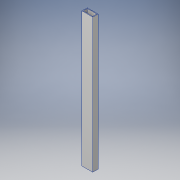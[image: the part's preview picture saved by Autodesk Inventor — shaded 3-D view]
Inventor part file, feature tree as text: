
AUTODESK INVENTOR PART (.ipt)
format: ipt  version: 2018 (Build 220112000, 112)  size: 110,080 bytes
history: native  units: in
note: dims shown in document units (in); Inventor stores cm internally (conversion verified against a paired STEP export)
features: extrude x2, sketch x2
ambient origin geometry x8: Origin, YZ Plane, XZ Plane, XY Plane, X Axis, Y Axis, Z Axis, Center Point
bodies: Solid1 (feature_tree)
feature tree (4):
  extrude  "Extrusion1"  Depth=2.0in
  extrude  "Extrusion2"  Depth=0.125in
  sketch  "Sketch1"  dims[d0=1.0in d1=2.0in]
  sketch  "Sketch2"  dims[d2=0.125in d3=0.125in d4=0.125in d5=0.125in d6=29.0in d7=0.0in d8=4.0in d9=0.0in]
